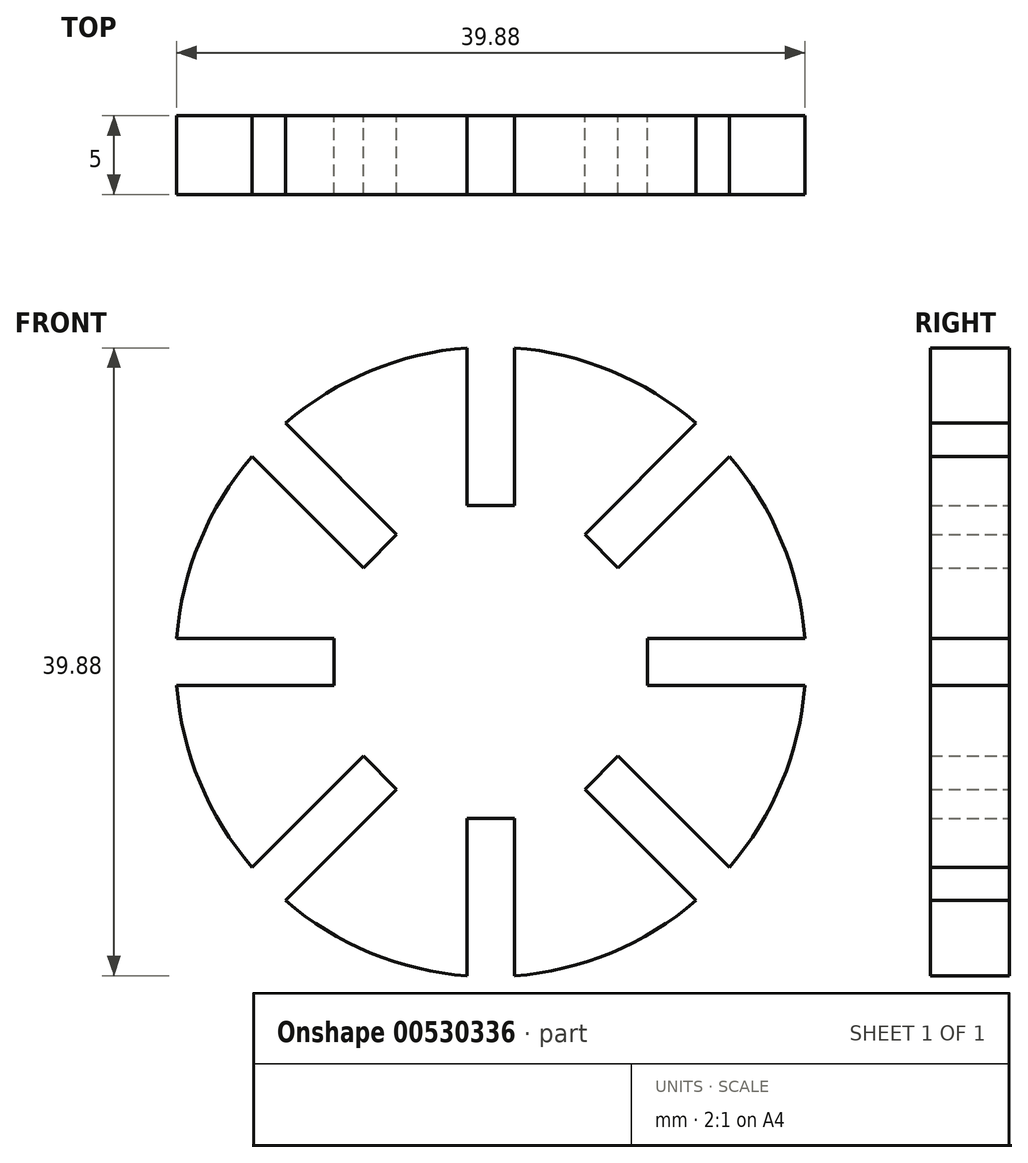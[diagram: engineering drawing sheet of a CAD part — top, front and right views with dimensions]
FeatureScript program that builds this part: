
annotation { "Feature Type Name" : "Feature", "Feature Type Description" : "" }
export const myFeature = defineFeature(function(context is Context, id is Id, definition is map)
    precondition{}
    {
        {
            var Q0;
            Q0=qCreatedBy(makeId("Front.planeOp"),FACE);
            var sketch = newSketch(context, id + "F0", { "sketchPlane" : qUnion([Q0])});
            skPoint(sketch, "E0", {"position": v(-1.5, 19.94) * mm});
            skPoint(sketch, "E1", {"position": v(1.5, 19.94) * mm});
            skLineSegment(sketch, "E2", {"start": v(-1.5, 19.94) * mm, "end": v(-1.5, 9.94) * mm});
            skLineSegment(sketch, "E3", {"start": v(1.5, 19.94) * mm, "end": v(1.5, 9.94) * mm});
            skLineSegment(sketch, "E4", {"start": v(-1.5, 9.94) * mm, "end": v(1.5, 9.94) * mm});
            skLineSegment(sketch, "E5.1.0", {"start": v(-15.16, 13.04) * mm, "end": v(-8.1, 5.97) * mm});
            skPoint(sketch, "E5.1.1", {"position": v(-13.04, 15.16) * mm});
            skPoint(sketch, "E5.1.3", {"position": v(-15.16, 13.04) * mm});
            skLineSegment(sketch, "E5.1.4", {"start": v(-13.04, 15.16) * mm, "end": v(-5.97, 8.1) * mm});
            skLineSegment(sketch, "E5.1.5", {"start": v(-8.1, 5.97) * mm, "end": v(-5.97, 8.1) * mm});
            skLineSegment(sketch, "E5.2.0", {"start": v(-19.94, -1.5) * mm, "end": v(-9.94, -1.5) * mm});
            skPoint(sketch, "E5.2.1", {"position": v(-19.94, 1.5) * mm});
            skArc(sketch, "E5.2.2", {"start": v(-19.94, -1.5) * mm, "mid": v(-18.48, -7.65) * mm, "end": v(-15.16, -13.04) * mm});
            skPoint(sketch, "E5.2.3", {"position": v(-19.94, -1.5) * mm});
            skLineSegment(sketch, "E5.2.4", {"start": v(-19.94, 1.5) * mm, "end": v(-9.94, 1.5) * mm});
            skLineSegment(sketch, "E5.2.5", {"start": v(-9.94, -1.5) * mm, "end": v(-9.94, 1.5) * mm});
            skLineSegment(sketch, "E5.3.0", {"start": v(-13.04, -15.16) * mm, "end": v(-5.97, -8.1) * mm});
            skPoint(sketch, "E5.3.1", {"position": v(-15.16, -13.04) * mm});
            skPoint(sketch, "E5.3.3", {"position": v(-13.04, -15.16) * mm});
            skLineSegment(sketch, "E5.3.4", {"start": v(-15.16, -13.04) * mm, "end": v(-8.1, -5.97) * mm});
            skLineSegment(sketch, "E5.3.5", {"start": v(-5.97, -8.1) * mm, "end": v(-8.1, -5.97) * mm});
            skLineSegment(sketch, "E5.4.0", {"start": v(1.5, -19.94) * mm, "end": v(1.5, -9.94) * mm});
            skPoint(sketch, "E5.4.1", {"position": v(-1.5, -19.94) * mm});
            skPoint(sketch, "E5.4.3", {"position": v(1.5, -19.94) * mm});
            skLineSegment(sketch, "E5.4.4", {"start": v(-1.5, -19.94) * mm, "end": v(-1.5, -9.94) * mm});
            skLineSegment(sketch, "E5.4.5", {"start": v(1.5, -9.94) * mm, "end": v(-1.5, -9.94) * mm});
            skLineSegment(sketch, "E5.5.0", {"start": v(15.16, -13.04) * mm, "end": v(8.1, -5.97) * mm});
            skPoint(sketch, "E5.5.1", {"position": v(13.04, -15.16) * mm});
            skArc(sketch, "E5.5.2", {"start": v(15.16, -13.04) * mm, "mid": v(18.48, -7.65) * mm, "end": v(19.94, -1.5) * mm});
            skPoint(sketch, "E5.5.3", {"position": v(15.16, -13.04) * mm});
            skLineSegment(sketch, "E5.5.4", {"start": v(13.04, -15.16) * mm, "end": v(5.97, -8.1) * mm});
            skLineSegment(sketch, "E5.5.5", {"start": v(8.1, -5.97) * mm, "end": v(5.97, -8.1) * mm});
            skLineSegment(sketch, "E5.6.0", {"start": v(19.94, 1.5) * mm, "end": v(9.94, 1.5) * mm});
            skPoint(sketch, "E5.6.1", {"position": v(19.94, -1.5) * mm});
            skPoint(sketch, "E5.6.3", {"position": v(19.94, 1.5) * mm});
            skLineSegment(sketch, "E5.6.4", {"start": v(19.94, -1.5) * mm, "end": v(9.94, -1.5) * mm});
            skLineSegment(sketch, "E5.6.5", {"start": v(9.94, 1.5) * mm, "end": v(9.94, -1.5) * mm});
            skLineSegment(sketch, "E5.7.0", {"start": v(13.04, 15.16) * mm, "end": v(5.97, 8.1) * mm});
            skPoint(sketch, "E5.7.1", {"position": v(15.16, 13.04) * mm});
            skPoint(sketch, "E5.7.3", {"position": v(13.04, 15.16) * mm});
            skLineSegment(sketch, "E5.7.4", {"start": v(15.16, 13.04) * mm, "end": v(8.1, 5.97) * mm});
            skLineSegment(sketch, "E5.7.5", {"start": v(5.97, 8.1) * mm, "end": v(8.1, 5.97) * mm});
            skPoint(sketch, "E5.center", {"position": v(0, 0) * mm});
            skArc(sketch, "E6.trimOffspring", {"start": v(-1.5, 19.94) * mm, "mid": v(-7.65, 18.48) * mm, "end": v(-13.04, 15.16) * mm});
            skArc(sketch, "E7.trimOffspring", {"start": v(-15.16, 13.04) * mm, "mid": v(-18.48, 7.65) * mm, "end": v(-19.94, 1.5) * mm});
            skArc(sketch, "E8.trimOffspring", {"start": v(13.04, 15.16) * mm, "mid": v(7.65, 18.48) * mm, "end": v(1.5, 19.94) * mm});
            skArc(sketch, "E9.trimOffspring", {"start": v(19.94, 1.5) * mm, "mid": v(18.48, 7.65) * mm, "end": v(15.16, 13.04) * mm});
            skArc(sketch, "E10.trimOffspring", {"start": v(1.5, -19.94) * mm, "mid": v(7.65, -18.48) * mm, "end": v(13.04, -15.16) * mm});
            skArc(sketch, "E11.trimOffspring", {"start": v(-13.04, -15.16) * mm, "mid": v(-7.65, -18.48) * mm, "end": v(-1.5, -19.94) * mm});
            skSolve(sketch);
        }
        {
            var Q0;
            Q0 = qSketchRegion(id + "F0", true);
            extrude(context, id + "F1", {"entities" : qUnion([Q0]), "depth" : 5 * mm, "offsetDistance" : 25 * mm});
        }
    });
